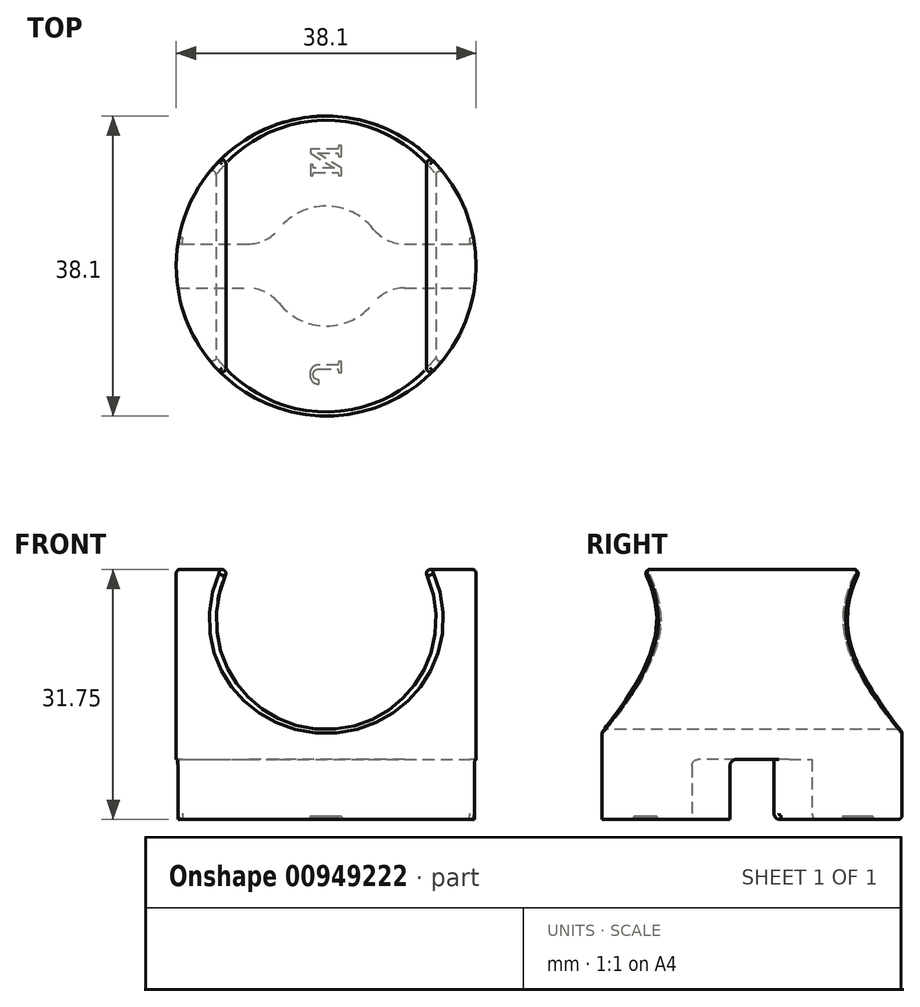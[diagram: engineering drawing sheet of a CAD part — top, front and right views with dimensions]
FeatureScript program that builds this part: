
annotation { "Feature Type Name" : "Feature", "Feature Type Description" : "" }
export const myFeature = defineFeature(function(context is Context, id is Id, definition is map)
    precondition{}
    {
        {
            var Q0;
            Q0=qCreatedBy(makeId("Top.planeOp"),FACE);
            var sketch = newSketch(context, id + "F0", { "sketchPlane" : qUnion([Q0])});
            skCircle(sketch, "E0", {"center": v(0, 0) * mm, "radius": 19.05 * mm});
            skSolve(sketch);
        }
        {
            var Q0;
            Q0=makeQuery(id+"F0.imprint","IMPRINT",FACE,{"disambiguationData":[TD([[makeQuery(id+"F0.imprint","IMPRINT",EDGE,{"derivedFrom":sQuery(id+"F0.wireOp",EDGE,"E0")}),1.0]])]});
            extrude(context, id + "F1", {"entities" : qUnion([Q0]), "depth" : 31.75 * mm, "offsetDistance" : 25.4 * mm});
        }
        {
            var Q0;
            Q0=qCreatedBy(makeId("Front.planeOp"),FACE);
            var sketch = newSketch(context, id + "F2", { "sketchPlane" : qUnion([Q0])});
            skCircle(sketch, "E1", {"center": v(0, 25.4) * mm, "radius": 13.97 * mm});
            skSolve(sketch);
        }
        {
            var Q0;
            Q0 = qSketchRegion(id + "F2", true);
            extrude(context, id + "F3", {"entities" : qUnion([Q0]), "operationType" : NewBodyOperationType.REMOVE, "endBound" : BoundingType.SYMMETRIC, "oppositeDirection" : true, "depth" : 50.8 * mm, "offsetDistance" : 25.4 * mm});
        }
        {
            var Q0;
            Q0=makeQuery(id+"F1.opExtrude","CAP_FACE",FACE,{"disambiguationData":[OSD([sQuery(id+"F0.wireOp",EDGE,"E0")])],"isStart":true});
            var sketch = newSketch(context, id + "F4", { "sketchPlane" : qUnion([Q0])});
            skCircle(sketch, "E2", {"center": v(0, 0) * mm, "radius": 7.62 * mm});
            skSolve(sketch);
        }
        {
            var Q0;
            Q0 = qSketchRegion(id + "F4", true);
            extrude(context, id + "F5", {"entities" : qUnion([Q0]), "operationType" : NewBodyOperationType.REMOVE, "oppositeDirection" : true, "depth" : 7.62 * mm, "offsetDistance" : 25.4 * mm});
        }
        {
            var Q0;
            Q0=qCreatedBy(makeId("Right.planeOp"),FACE);
            var sketch = newSketch(context, id + "F6", { "sketchPlane" : qUnion([Q0])});
            skLineSegment(sketch, "E3", {"start": v(2.8, 0) * mm, "end": v(2.8, 7.62) * mm});
            skLineSegment(sketch, "E4", {"start": v(2.8, 7.62) * mm, "end": v(0, 7.62) * mm});
            skLineSegment(sketch, "E5.MirrorCS", {"start": v(-2.8, 0) * mm, "end": v(-2.8, 7.62) * mm});
            skLineSegment(sketch, "E6.MirrorCS", {"start": v(-2.8, 7.62) * mm, "end": v(0, 7.62) * mm});
            skLineSegment(sketch, "E7", {"start": v(2.8, 0) * mm, "end": v(-2.8, 0) * mm});
            skLineSegment(sketch, "E8", {"start": v(-7.62, 7.62) * mm, "end": v(7.62, 7.62) * mm});
            skSolve(sketch);
        }
        {
            var Q0;
            Q0 = qSketchRegion(id + "F6", true);
            extrude(context, id + "F7", {"entities" : qUnion([Q0]), "operationType" : NewBodyOperationType.REMOVE, "endBound" : BoundingType.SYMMETRIC, "oppositeDirection" : true, "depth" : 50.8 * mm, "offsetDistance" : 25.4 * mm});
        }
        {
            var Q0;
            Q0=makeQuery(id+"F7.boolean.opBoolean","INTERSECT",EDGE,{"disambiguationData":[OD(0.0)],"derivedFrom":[makeQuery(id+"F5.boolean.opBoolean","COPY",FACE,{"derivedFrom":makeQuery(id+"F5.opExtrude","SWEPT_FACE",FACE,{"disambiguationData":[OSD([sQuery(id+"F4.wireOp",EDGE,"E2")])]})}),makeQuery(id+"F7.opExtrude","SWEPT_FACE",FACE,{"disambiguationData":[OSD([sQuery(id+"F6.wireOp",EDGE,"E3")])]})]});
            var Q1;
            Q1=makeQuery(id+"F7.boolean.opBoolean","INTERSECT",EDGE,{"disambiguationData":[OD(1.0)],"derivedFrom":[makeQuery(id+"F5.boolean.opBoolean","COPY",FACE,{"derivedFrom":makeQuery(id+"F5.opExtrude","SWEPT_FACE",FACE,{"disambiguationData":[OSD([sQuery(id+"F4.wireOp",EDGE,"E2")])]})}),makeQuery(id+"F7.opExtrude","SWEPT_FACE",FACE,{"disambiguationData":[OSD([sQuery(id+"F6.wireOp",EDGE,"E3")])]})]});
            var Q2;
            Q2=makeQuery(id+"F7.boolean.opBoolean","INTERSECT",EDGE,{"disambiguationData":[OD(0.0)],"derivedFrom":[makeQuery(id+"F5.boolean.opBoolean","COPY",FACE,{"derivedFrom":makeQuery(id+"F5.opExtrude","SWEPT_FACE",FACE,{"disambiguationData":[OSD([sQuery(id+"F4.wireOp",EDGE,"E2")])]})}),makeQuery(id+"F7.opExtrude","SWEPT_FACE",FACE,{"disambiguationData":[OSD([sQuery(id+"F6.wireOp",EDGE,"E5.MirrorCS")])]})]});
            var Q3;
            Q3=makeQuery(id+"F7.boolean.opBoolean","INTERSECT",EDGE,{"disambiguationData":[OD(1.0)],"derivedFrom":[makeQuery(id+"F5.boolean.opBoolean","COPY",FACE,{"derivedFrom":makeQuery(id+"F5.opExtrude","SWEPT_FACE",FACE,{"disambiguationData":[OSD([sQuery(id+"F4.wireOp",EDGE,"E2")])]})}),makeQuery(id+"F7.opExtrude","SWEPT_FACE",FACE,{"disambiguationData":[OSD([sQuery(id+"F6.wireOp",EDGE,"E5.MirrorCS")])]})]});
            fillet(context, id + "F8", {"entities" : qUnion([Q0, Q1, Q2, Q3]), "radius" : 5.08 * mm, "tangentPropagation" : true, "allowEdgeOverflow" : false});
        }
        {
            var Q0;
            Q0=makeQuery(id+"F7.boolean.opBoolean","COPY",EDGE,{"disambiguationData":[OD(1.0)],"derivedFrom":makeQuery(id+"F7.opExtrude","SWEPT_EDGE",EDGE,{"disambiguationData":[OSD([sQuery(id+"F6.wireOp",EDGE,"E5.MirrorCS"),sQuery(id+"F6.wireOp",EDGE,"E8")])]})});
            var Q1;
            Q1=makeQuery(id+"F7.boolean.opBoolean","COPY",EDGE,{"disambiguationData":[OD(1.0)],"derivedFrom":makeQuery(id+"F7.opExtrude","SWEPT_EDGE",EDGE,{"disambiguationData":[OSD([sQuery(id+"F6.wireOp",EDGE,"E3"),sQuery(id+"F6.wireOp",EDGE,"E8")])]})});
            var Q2;
            Q2=makeQuery(id+"F7.boolean.opBoolean","COPY",EDGE,{"disambiguationData":[OD(1.0)],"derivedFrom":makeQuery(id+"F7.opExtrude","SWEPT_EDGE",EDGE,{"disambiguationData":[OSD([sQuery(id+"F6.wireOp",EDGE,"E5.MirrorCS"),sQuery(id+"F6.wireOp",EDGE,"E7")])]})});
            var Q3;
            Q3=makeQuery(id+"F7.boolean.opBoolean","COPY",EDGE,{"disambiguationData":[OD(1.0)],"derivedFrom":makeQuery(id+"F7.opExtrude","SWEPT_EDGE",EDGE,{"disambiguationData":[OSD([sQuery(id+"F6.wireOp",EDGE,"E3"),sQuery(id+"F6.wireOp",EDGE,"E7")])]})});
            fillet(context, id + "F9", {"entities" : qUnion([Q0, Q1, Q2, Q3]), "radius" : 0.76 * mm, "tangentPropagation" : true, "allowEdgeOverflow" : false});
        }
        {
            var Q0;
            {var subQ0=sQuery(id+"F0.wireOp",EDGE,"E0");Q0=makeQuery(id+"F7.boolean.opBoolean","SPLIT",EDGE,{"disambiguationData":[TD([makeQuery(id+"F7.opExtrude","SWEPT_FACE",FACE,{"disambiguationData":[OSD([sQuery(id+"F6.wireOp",EDGE,"E3")])]})])],"derivedFrom":makeQuery(id+"F1.opExtrude","CAP_EDGE",EDGE,{"disambiguationData":[OSD([subQ0])],"isStart":true})});}
            fillet(context, id + "F10", {"entities" : qUnion([Q0]), "radius" : 0.5 * mm, "tangentPropagation" : true, "allowEdgeOverflow" : false});
        }
        {
            var Q0;
            Q0=makeQuery(id+"F3.boolean.opBoolean","INTERSECT",EDGE,{"disambiguationData":[OD(1.0)],"derivedFrom":[makeQuery(id+"F1.opExtrude","SWEPT_FACE",FACE,{"disambiguationData":[OSD([sQuery(id+"F0.wireOp",EDGE,"E0")])]}),makeQuery(id+"F3.opExtrude","SWEPT_FACE",FACE,{"disambiguationData":[OSD([sQuery(id+"F2.wireOp",EDGE,"E1")])]})]});
            var Q1;
            Q1=makeQuery(id+"F3.boolean.opBoolean","INTERSECT",EDGE,{"disambiguationData":[OD(0.0)],"derivedFrom":[makeQuery(id+"F1.opExtrude","SWEPT_FACE",FACE,{"disambiguationData":[OSD([sQuery(id+"F0.wireOp",EDGE,"E0")])]}),makeQuery(id+"F3.opExtrude","SWEPT_FACE",FACE,{"disambiguationData":[OSD([sQuery(id+"F2.wireOp",EDGE,"E1")])]})]});
            var Q2;
            Q2=makeQuery(id+"F3.boolean.opBoolean","SPLIT",EDGE,{"disambiguationData":[OD(1.0)],"derivedFrom":makeQuery(id+"F1.opExtrude","CAP_EDGE",EDGE,{"disambiguationData":[OSD([sQuery(id+"F0.wireOp",EDGE,"E0")])],"isStart":false})});
            var Q3;
            Q3=makeQuery(id+"F3.boolean.opBoolean","INTERSECT",EDGE,{"disambiguationData":[OD(1.0)],"derivedFrom":[makeQuery(id+"F1.opExtrude","CAP_FACE",FACE,{"disambiguationData":[OSD([sQuery(id+"F0.wireOp",EDGE,"E0")])],"isStart":false}),makeQuery(id+"F3.opExtrude","SWEPT_FACE",FACE,{"disambiguationData":[OSD([sQuery(id+"F2.wireOp",EDGE,"E1")])]})]});
            var Q4;
            Q4=makeQuery(id+"F3.boolean.opBoolean","SPLIT",EDGE,{"disambiguationData":[OD(0.0)],"derivedFrom":makeQuery(id+"F1.opExtrude","CAP_EDGE",EDGE,{"disambiguationData":[OSD([sQuery(id+"F0.wireOp",EDGE,"E0")])],"isStart":false})});
            var Q5;
            Q5=makeQuery(id+"F3.boolean.opBoolean","INTERSECT",EDGE,{"disambiguationData":[OD(0.0)],"derivedFrom":[makeQuery(id+"F1.opExtrude","CAP_FACE",FACE,{"disambiguationData":[OSD([sQuery(id+"F0.wireOp",EDGE,"E0")])],"isStart":false}),makeQuery(id+"F3.opExtrude","SWEPT_FACE",FACE,{"disambiguationData":[OSD([sQuery(id+"F2.wireOp",EDGE,"E1")])]})]});
            fillet(context, id + "F11", {"entities" : qUnion([Q0, Q1, Q2, Q3, Q4, Q5]), "radius" : 0.5 * mm, "tangentPropagation" : true, "allowEdgeOverflow" : false});
        }
        {
            var Q0;
            {var subQ0=sQuery(id+"F0.wireOp",EDGE,"E0");Q0=makeQuery(id+"F7.boolean.opBoolean","SPLIT",FACE,{"disambiguationData":[TD([makeQuery(id+"F7.opExtrude","SWEPT_FACE",FACE,{"disambiguationData":[OSD([sQuery(id+"F6.wireOp",EDGE,"E5.MirrorCS")])]})])],"derivedFrom":makeQuery(id+"F1.opExtrude","CAP_FACE",FACE,{"disambiguationData":[OSD([subQ0])],"isStart":true})});}
            var sketch = newSketch(context, id + "F12", { "sketchPlane" : qUnion([Q0])});
            skText(sketch, "E9", { "text": "J\n", "fontName": "RobotoSlab-Regular.ttf"});
            skPoint(sketch, "E10", {"position": v(0, 15.15) * mm});
            skLineSegment(sketch, "E11", {"start": v(0, 18.54) * mm, "end": v(0, 8.38) * mm, "construction": true});
            skPoint(sketch, "E12", {"position": v(0, 13.46) * mm});
            skText(sketch, "E13", { "text": "N\n", "fontName": "RobotoSlab-Regular.ttf"});
            skLineSegment(sketch, "E14.0.0", {"start": v(-9.96, -3.56) * mm, "end": v(-18.2, -3.56) * mm, "construction": true});
            skArc(sketch, "E14.0.1", {"start": v(-18.2, -3.56) * mm, "mid": v(0, -18.54) * mm, "end": v(18.2, -3.56) * mm, "construction": true});
            skLineSegment(sketch, "E14.0.2", {"start": v(18.2, -3.56) * mm, "end": v(9.96, -3.56) * mm, "construction": true});
            skArc(sketch, "E14.0.3", {"start": v(9.96, -3.56) * mm, "mid": v(8.08, -3.99) * mm, "end": v(6.58, -5.2) * mm, "construction": true});
            skArc(sketch, "E14.0.4", {"start": v(6.58, -5.2) * mm, "mid": v(0, -8.38) * mm, "end": v(-6.58, -5.2) * mm, "construction": true});
            skArc(sketch, "E14.0.5", {"start": v(-6.58, -5.2) * mm, "mid": v(-8.08, -3.99) * mm, "end": v(-9.96, -3.56) * mm, "construction": true});
            skLineSegment(sketch, "E15", {"start": v(0, -8.38) * mm, "end": v(0, -18.54) * mm, "construction": true});
            skPoint(sketch, "E16", {"position": v(0, -13.46) * mm});
            const initialGuessF12  = {"E9": [-0.002, 0.01515, 0, -1, 0.00399], "E13": [-0.002, -0.01127, 0, -1, 0.00399]};
            skSetInitialGuess(sketch, initialGuessF12);
            skSolve(sketch);
        }
        {
            var Q0;
            Q0 = qSketchRegion(id + "F12", true);
            extrude(context, id + "F13", {"entities" : qUnion([Q0]), "operationType" : NewBodyOperationType.REMOVE, "oppositeDirection" : true, "depth" : 0.4 * mm, "offsetDistance" : 25.4 * mm});
        }
    });
